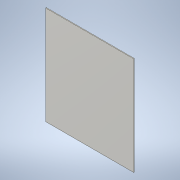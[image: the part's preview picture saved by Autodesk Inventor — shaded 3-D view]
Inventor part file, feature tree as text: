
AUTODESK INVENTOR PART (.ipt)
format: ipt  version: 2022 (Build 260153000, 153)  size: 91,136 bytes
history: native  units: mm
features: other x1, extrude x1, sketch x1
ambient origin geometry x8: Origin, YZ Plane, XZ Plane, XY Plane, X Axis, Y Axis, Z Axis, Center Point
bodies: Body1 (feature_tree)
feature tree (3):
  other  "Sólido1"
  extrude  "Extrusão1"  Depth=280.0mm
  sketch  "Esboço1"  dims[d0=250.0mm d1=280.0mm d2=2.0mm d3=0.0mm]
